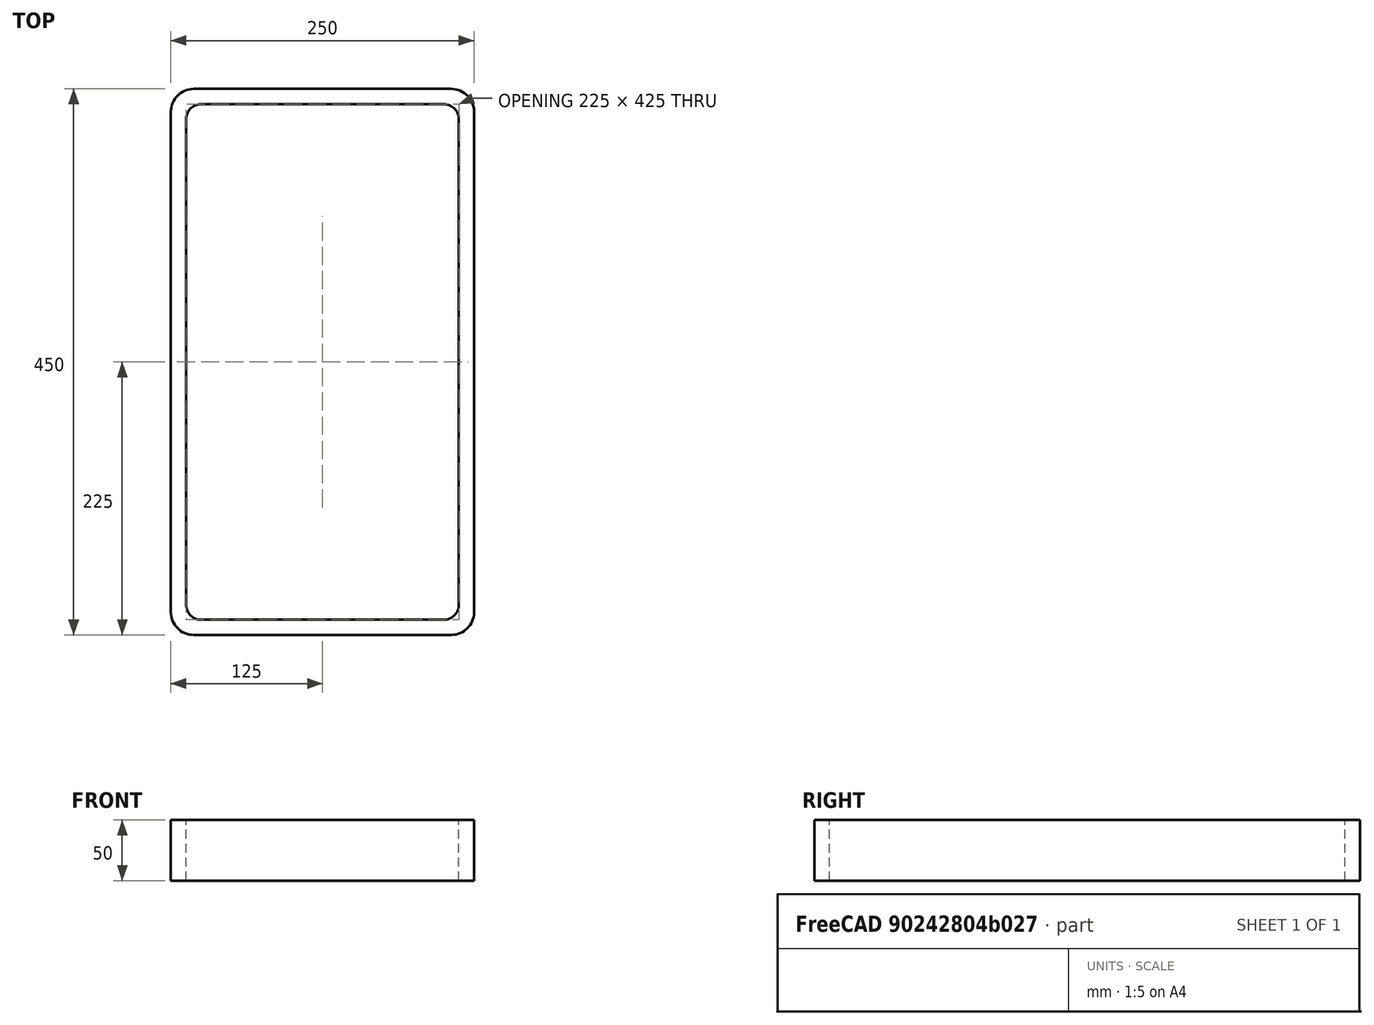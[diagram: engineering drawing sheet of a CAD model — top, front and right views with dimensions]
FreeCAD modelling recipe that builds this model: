
FCSTD DOCUMENT  (FreeCAD 0.15R4671 (Git))
Label: Rectangular hollow section 450x250x12.5 EN10219 S235JRH
License: All rights reserved
LicenseURL: http://en.wikipedia.org/wiki/All_rights_reserved
objects: Sketcher::SketchObject×1, Part::Extrusion×1
note: 2 computed .brp shape members not serialized (recipe doc carries the construction recipe); baked Part::Feature solids carry a one-line shape summary decoded from their .brp

FEATURE [Sketcher::SketchObject] Sketch
  sketch-geometry (16):
    g0: LineSegment StartX=-100 StartY=212.5 StartZ=0 EndX=100 EndY=212.5 EndZ=0
    g1: LineSegment StartX=112.5 StartY=200 StartZ=0 EndX=112.5 EndY=-200 EndZ=0
    g2: LineSegment StartX=100 StartY=-212.5 StartZ=0 EndX=-100 EndY=-212.5 EndZ=0
    g3: LineSegment StartX=-112.5 StartY=-200 StartZ=0 EndX=-112.5 EndY=200 EndZ=0
    g4: LineSegment StartX=-106.25 StartY=225 StartZ=0 EndX=106.25 EndY=225 EndZ=0
    g5: LineSegment StartX=125 StartY=206.25 StartZ=0 EndX=125 EndY=-206.25 EndZ=0
    g6: LineSegment StartX=106.25 StartY=-225 StartZ=0 EndX=-106.25 EndY=-225 EndZ=0
    g7: LineSegment StartX=-125 StartY=-206.25 StartZ=0 EndX=-125 EndY=206.25 EndZ=0
    g8: ArcOfCircle CenterX=-100 CenterY=200 CenterZ=0 NormalX=0 NormalY=0 NormalZ=1 Radius=12.5 StartAngle=1.5708 EndAngle=3.14159
    g9: ArcOfCircle CenterX=100 CenterY=200 CenterZ=0 NormalX=0 NormalY=0 NormalZ=1 Radius=12.5 StartAngle=0 EndAngle=1.5708
    g10: ArcOfCircle CenterX=100 CenterY=-200 CenterZ=0 NormalX=0 NormalY=0 NormalZ=1 Radius=12.5 StartAngle=4.71239 EndAngle=6.28319
    g11: ArcOfCircle CenterX=-100 CenterY=-200 CenterZ=0 NormalX=0 NormalY=0 NormalZ=1 Radius=12.5 StartAngle=3.14159 EndAngle=4.71239
    g12: ArcOfCircle CenterX=106.25 CenterY=206.25 CenterZ=0 NormalX=0 NormalY=0 NormalZ=1 Radius=18.75 StartAngle=0 EndAngle=1.5708
    g13: ArcOfCircle CenterX=106.25 CenterY=-206.25 CenterZ=0 NormalX=0 NormalY=0 NormalZ=1 Radius=18.75 StartAngle=4.71239 EndAngle=6.28319
    g14: ArcOfCircle CenterX=-106.25 CenterY=-206.25 CenterZ=0 NormalX=0 NormalY=0 NormalZ=1 Radius=18.75 StartAngle=3.14159 EndAngle=4.71239
    g15: ArcOfCircle CenterX=-106.25 CenterY=206.25 CenterZ=0 NormalX=0 NormalY=0 NormalZ=1 Radius=18.75 StartAngle=1.5708 EndAngle=3.14159
  constraints (36):
    c: Horizontal(g2)
    c: Vertical(g3)
    c: Horizontal(g6)
    c: Vertical(g7)
    c: Tangent(g3,g8) = 1.5708
    c: Tangent(g0,g8) = 1.5708
    c: Tangent(g0,g9) = 1.5708
    c: Tangent(g1,g9) = 1.5708
    c: Tangent(g1,g10) = 1.5708
    c: Tangent(g2,g10) = 1.5708
    c: Tangent(g2,g11) = 1.5708
    c: Tangent(g3,g11) = 1.5708
    c: Tangent(g4,g12) = 1.5708
    c: Tangent(g5,g12) = 1.5708
    c: Tangent(g5,g13) = 1.5708
    c: Tangent(g6,g13) = 1.5708
    c: Tangent(g6,g14) = 1.5708
    c: Tangent(g7,g14) = 1.5708
    c: Tangent(g7,g15) = 1.5708
    c: Tangent(g4,g15) = 1.5708
    c: Equal(g9,g8)
    c: Equal(g9,g11)
    c: Equal(g9,g10)
    c: Equal(g12,g15)
    c: Equal(g12,g14)
    c: Equal(g12,g13)
    c: Symmetric(g4,g6,g-1)
    c: Symmetric(g7,g5,g-2)
    c: DistanceY(g4,g6) = -450
    c: DistanceX(g7,g5) = 250
    c: Symmetric(g3,g1,g-2)
    c: Symmetric(g0,g2,g-1)
    c: DistanceY(g0,g4) = 12.5
    c: DistanceX(g5,g1) = -12.5
    c: Radius(g9) = 12.5
    c: Radius(g12) = 18.75
FEATURE [Part::Extrusion] Extrude  label="Rectangular hollow section 450x250x12.5 EN10219 S235JRH"
  Base = -> Sketch
  Dir = (0,0,50)
  Solid = true
